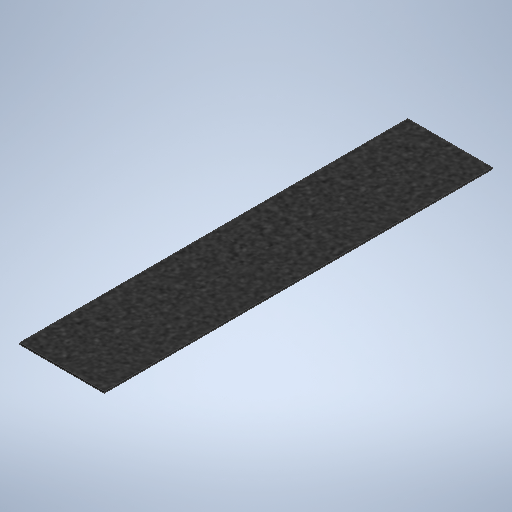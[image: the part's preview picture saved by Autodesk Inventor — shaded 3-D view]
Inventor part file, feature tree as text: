
AUTODESK INVENTOR PART (.ipt)
format: ipt  version: 2025.1 (Build 291241020, 241B)  size: 274,432 bytes
history: native  units: in
note: dims shown in document units (in); Inventor stores cm internally (conversion verified against a paired STEP export)
features: extrude x1, sketch x1
ambient origin geometry x8: Origin, YZ Plane, XZ Plane, XY Plane, X Axis, Y Axis, Z Axis, Center Point
bodies: Solid1 (feature_tree)
feature tree (2):
  extrude  "Extrusion1"  Depth=29.875in
  sketch  "Sketch1"  dims[d0=6.5in d1=29.875in d2=0.125in d3=0.0in]
